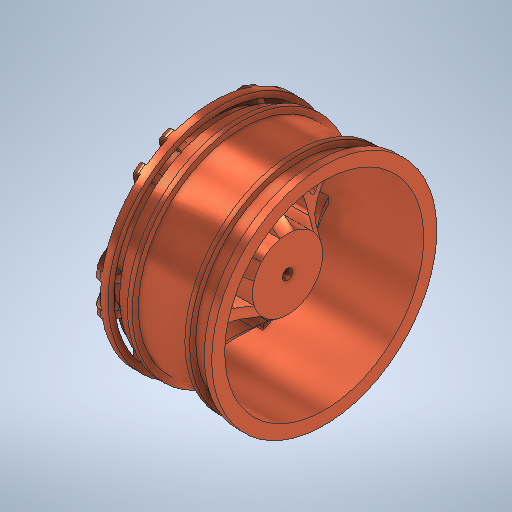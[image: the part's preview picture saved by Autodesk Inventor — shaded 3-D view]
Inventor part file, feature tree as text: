
AUTODESK INVENTOR PART (.ipt)
format: ipt  version: 2025 (Build 290162000, 162)  size: 1,631,232 bytes
history: native  units: in
note: dims shown in document units (in); Inventor stores cm internally (conversion verified against a paired STEP export)
features: sketch x8, fillet x4, revolve x3, extrude x3, pattern_circular x2, thicken_offset x1, hole x1
ambient origin geometry x8: Origin, YZ Plane, XZ Plane, XY Plane, X Axis, Y Axis, Z Axis, Center Point
bodies: Solid1 (feature_tree)
feature tree (22):
  revolve  "Revolution1"  [1 undecoded]
  extrude  "Extrusion1"  Depth=0.465in
  thicken_offset  "Thicken1"
  revolve  "Revolution2"  [1 undecoded]
  sketch  "Sketch4"  dims[d23=0.9843in d24=0.0in]
  extrude  "Extrusion2"  Depth=0.6598in
  fillet  "Fillet1"  Radius=2.0449in
  fillet  "Fillet2"  Radius=1.5489in
  pattern_circular  "Circular Pattern1"  Count=6 Angle=360.0deg
  pattern_circular  "Circular Pattern2"  [2 undecoded]
  revolve  "Revolution3"  Angle=90.0deg
  extrude  "Extrusion3"  Depth=0.0394in TaperAngle=0.0deg
  fillet  "Fillet3"  Radius=0.0787in
  fillet  "Fillet4"  Radius=0.0787in
  hole  "Hole2"  [1 undecoded]
  sketch  "Sketch1"  dims[d0=1.0224in d1=1.0449in]
  sketch  "Sketch2"  dims[d2=0.3299in d3=0.465in]
  sketch  "Sketch Circular Pattern2"  dims[d4=0.1142in d5=0.3299in]
  sketch  "Sketch3"  dims[d6=360.0deg d8=0.6598in d9=2.0449in d18=1.5489in d19=2.3622in d21=360.0deg]
  sketch  "Sketch5"  dims[d25=0.1575in d26=0.1969in]
  sketch  "Sketch6"  dims[d27=0.9249in]
  sketch  "Sketch7"  dims[d28=1.0224in d31=0.1224in d32=90.0deg d33=0.9843in d34=0.0in d35=0.0787in d36=0.0787in d37=2.3622in d38=360.0deg d40=2.3622in d41=360.0deg d43=0.9249in d44=0.0701in d45=0.0799in d48=0.0575in d49=0.1598in d50=0.0449in d51=90.0deg d52=0.0381in d53=0.0394in d54=0.0in d55=0.0394in d56=0.0394in d64=0.0984in d65=0.2362in d66=0.1575in d67=0.0787in d68=90.0deg d69=0.315in d70=0.8108in]
note: 5 required parameter values undecoded (feature->parameter linkage not recoverable at this tier; creation-order binding heuristic only, values carry confidence <= 0.55)